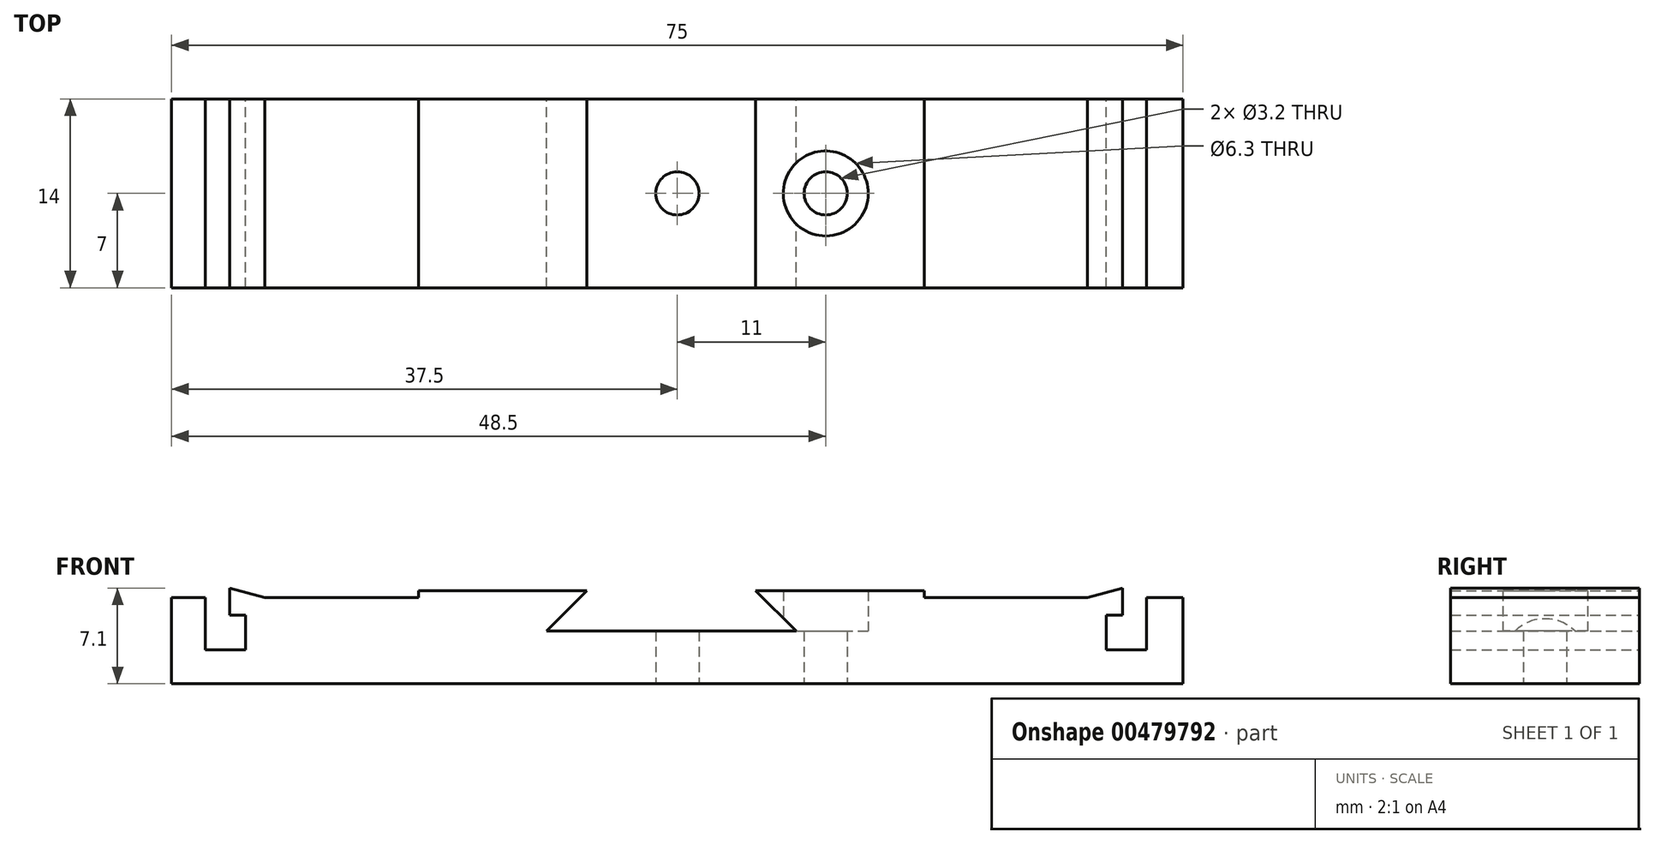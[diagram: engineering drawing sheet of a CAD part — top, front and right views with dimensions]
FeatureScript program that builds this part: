
annotation { "Feature Type Name" : "Feature", "Feature Type Description" : "" }
export const myFeature = defineFeature(function(context is Context, id is Id, definition is map)
    precondition{}
    {
        {
            var Q0;
            Q0=qCreatedBy(makeId("Front.planeOp"),FACE);
            var sketch = newSketch(context, id + "F0", { "sketchPlane" : qUnion([Q0])});
            skLineSegment(sketch, "E0", {"start": v(0, 0) * mm, "end": v(-75, 0) * mm});
            skLineSegment(sketch, "E1", {"start": v(-75, 0) * mm, "end": v(-75, 6.4) * mm});
            skLineSegment(sketch, "E2", {"start": v(-75, 6.4) * mm, "end": v(-72.5, 6.4) * mm});
            skLineSegment(sketch, "E3", {"start": v(-72.5, 6.4) * mm, "end": v(-72.5, 2.5) * mm});
            skLineSegment(sketch, "E4", {"start": v(-72.5, 2.5) * mm, "end": v(-69.5, 2.5) * mm});
            skLineSegment(sketch, "E5", {"start": v(-69.5, 2.5) * mm, "end": v(-69.5, 5.1) * mm});
            skLineSegment(sketch, "E6", {"start": v(-69.5, 5.1) * mm, "end": v(-70.7, 5.1) * mm});
            skLineSegment(sketch, "E7", {"start": v(-70.7, 5.1) * mm, "end": v(-70.7, 6.4) * mm});
            skLineSegment(sketch, "E8", {"start": v(-68.1, 6.4) * mm, "end": v(-56.7, 6.4) * mm});
            skLineSegment(sketch, "E9", {"start": v(-44.7, 6.4) * mm, "end": v(-47.2, 3.9) * mm});
            skLineSegment(sketch, "E10", {"start": v(-47.2, 3.9) * mm, "end": v(-28.7, 3.9) * mm});
            skLineSegment(sketch, "E11", {"start": v(-28.7, 3.9) * mm, "end": v(-31.2, 6.4) * mm});
            skLineSegment(sketch, "E12", {"start": v(-19.2, 6.4) * mm, "end": v(-7.1, 6.4) * mm});
            skLineSegment(sketch, "E13", {"start": v(-4.5, 6.4) * mm, "end": v(-4.5, 5.1) * mm});
            skLineSegment(sketch, "E14", {"start": v(-4.5, 5.1) * mm, "end": v(-5.7, 5.1) * mm});
            skLineSegment(sketch, "E15", {"start": v(-5.7, 5.1) * mm, "end": v(-5.7, 2.5) * mm});
            skLineSegment(sketch, "E16", {"start": v(-5.7, 2.5) * mm, "end": v(-2.7, 2.5) * mm});
            skLineSegment(sketch, "E17", {"start": v(-2.7, 2.5) * mm, "end": v(-2.7, 6.4) * mm});
            skLineSegment(sketch, "E18", {"start": v(-2.7, 6.4) * mm, "end": v(0, 6.4) * mm});
            skLineSegment(sketch, "E19", {"start": v(0, 6.4) * mm, "end": v(0, 0) * mm});
            skLineSegment(sketch, "E20", {"start": v(-44.7, 6.4) * mm, "end": v(-44.2, 6.9) * mm});
            skLineSegment(sketch, "E21", {"start": v(-44.2, 6.9) * mm, "end": v(-56.7, 6.9) * mm});
            skLineSegment(sketch, "E22", {"start": v(-56.7, 6.9) * mm, "end": v(-56.7, 6.4) * mm});
            skLineSegment(sketch, "E23", {"start": v(-31.2, 6.4) * mm, "end": v(-31.7, 6.9) * mm});
            skLineSegment(sketch, "E24", {"start": v(-31.7, 6.9) * mm, "end": v(-19.2, 6.9) * mm});
            skLineSegment(sketch, "E25", {"start": v(-19.2, 6.9) * mm, "end": v(-19.2, 6.4) * mm});
            skLineSegment(sketch, "E26", {"start": v(-70.7, 6.4) * mm, "end": v(-70.7, 7.1) * mm});
            skLineSegment(sketch, "E27", {"start": v(-70.7, 7.1) * mm, "end": v(-68.1, 6.4) * mm});
            skLineSegment(sketch, "E28", {"start": v(-4.5, 6.4) * mm, "end": v(-4.5, 7.1) * mm});
            skLineSegment(sketch, "E29", {"start": v(-4.5, 7.1) * mm, "end": v(-7.1, 6.4) * mm});
            skSolve(sketch);
        }
        {
            var Q0;
            Q0=makeQuery(id+"F0.imprint","IMPRINT",FACE,{"disambiguationData":[TD([[makeQuery(id+"F0.imprint","IMPRINT",EDGE,{"derivedFrom":sQuery(id+"F0.wireOp",EDGE,"E0")}),-1.0]])]});
            extrude(context, id + "F1", {"entities" : qUnion([Q0]), "endBound" : BoundingType.SYMMETRIC, "depth" : 14 * mm});
        }
        {
            var Q0;
            Q0=makeQuery(id+"F1.opExtrude","SWEPT_FACE",FACE,{"disambiguationData":[OSD([sQuery(id+"F0.wireOp",EDGE,"E0")])]});
            var sketch = newSketch(context, id + "F2", { "sketchPlane" : qUnion([Q0])});
            skCircle(sketch, "E30", {"center": v(-37.5, 0) * mm, "radius": 1.6 * mm});
            skPoint(sketch, "E30.centerSnap0", {"position": v(-37.5, -7) * mm});
            skCircle(sketch, "E31", {"center": v(-26.5, 0) * mm, "radius": 1.6 * mm});
            skCircle(sketch, "E32", {"center": v(-26.5, 0) * mm, "radius": 3.15 * mm});
            skSolve(sketch);
        }
        {
            var Q0;
            Q0=makeQuery(id+"F2.imprint","IMPRINT",FACE,{"disambiguationData":[TD([[makeQuery(id+"F2.imprint","IMPRINT",EDGE,{"derivedFrom":sQuery(id+"F2.wireOp",EDGE,"E30")}),1.0]])]});
            var Q1;
            Q1=makeQuery(id+"F2.imprint","IMPRINT",FACE,{"disambiguationData":[TD([[makeQuery(id+"F2.imprint","IMPRINT",EDGE,{"derivedFrom":sQuery(id+"F2.wireOp",EDGE,"E31")}),1.0]])]});
            extrude(context, id + "F3", {"entities" : qUnion([Q0, Q1]), "operationType" : NewBodyOperationType.REMOVE, "oppositeDirection" : true, "depth" : 25 * mm});
        }
        {
            var Q0;
            Q0=makeQuery(id+"F2.imprint","IMPRINT",FACE,{"disambiguationData":[TD([[makeQuery(id+"F2.imprint","IMPRINT",EDGE,{"derivedFrom":sQuery(id+"F2.wireOp",EDGE,"E31")}),-1.0]])]});
            extrude(context, id + "F4", {"entities" : qUnion([Q0]), "operationType" : NewBodyOperationType.REMOVE, "oppositeDirection" : true, "depth" : 25 * mm, "hasSecondDirection" : true, "secondDirectionOppositeDirection" : true, "secondDirectionDepth" : 3.9 * mm});
        }
    });
